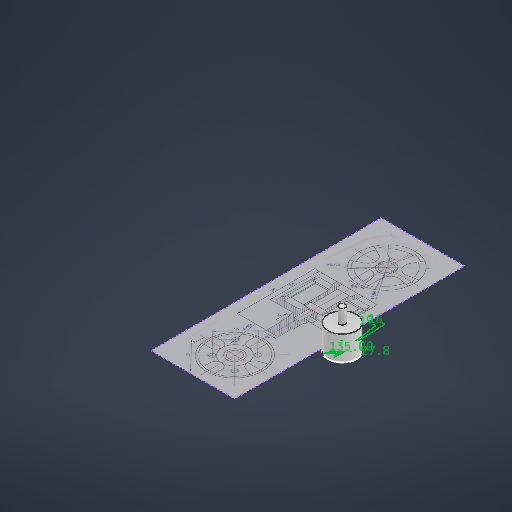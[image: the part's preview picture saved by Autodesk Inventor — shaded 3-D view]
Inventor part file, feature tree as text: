
AUTODESK INVENTOR PART (.ipt)
format: ipt  version: 2025 (Build 290162010, 162A)  size: 302,080 bytes
history: native  units: mm
features: sketch x2, extrude x2, hole x1, other x1
ambient origin geometry x8: Origin, YZ Plane, XZ Plane, XY Plane, X Axis, Y Axis, Z Axis, Center Point
bodies: Solid1 (feature_tree)
feature tree (6):
  sketch  "Sketch1"  dims[d7=27.8mm d8=16.0mm]
  extrude  "Extrusion1"  Depth=16.0mm
  hole  "Hole1"  [1 undecoded]
  extrude  "Extrusion2"  Depth=24.0mm TaperAngle=0.0deg
  other  "Image1"
  sketch  "Sketch2"  dims[d9=19.0mm d10=135.0deg d16=24.0mm d17=0.0mm d18=3.0mm d19=6.0mm d20=15.875mm d21=2.0mm d22=90.0deg d23=4.0mm d24=0.0mm d25=6.0mm d26=14.0mm d27=0.0mm]
note: 1 required parameter value undecoded (feature->parameter linkage not recoverable at this tier; creation-order binding heuristic only, values carry confidence <= 0.55)
